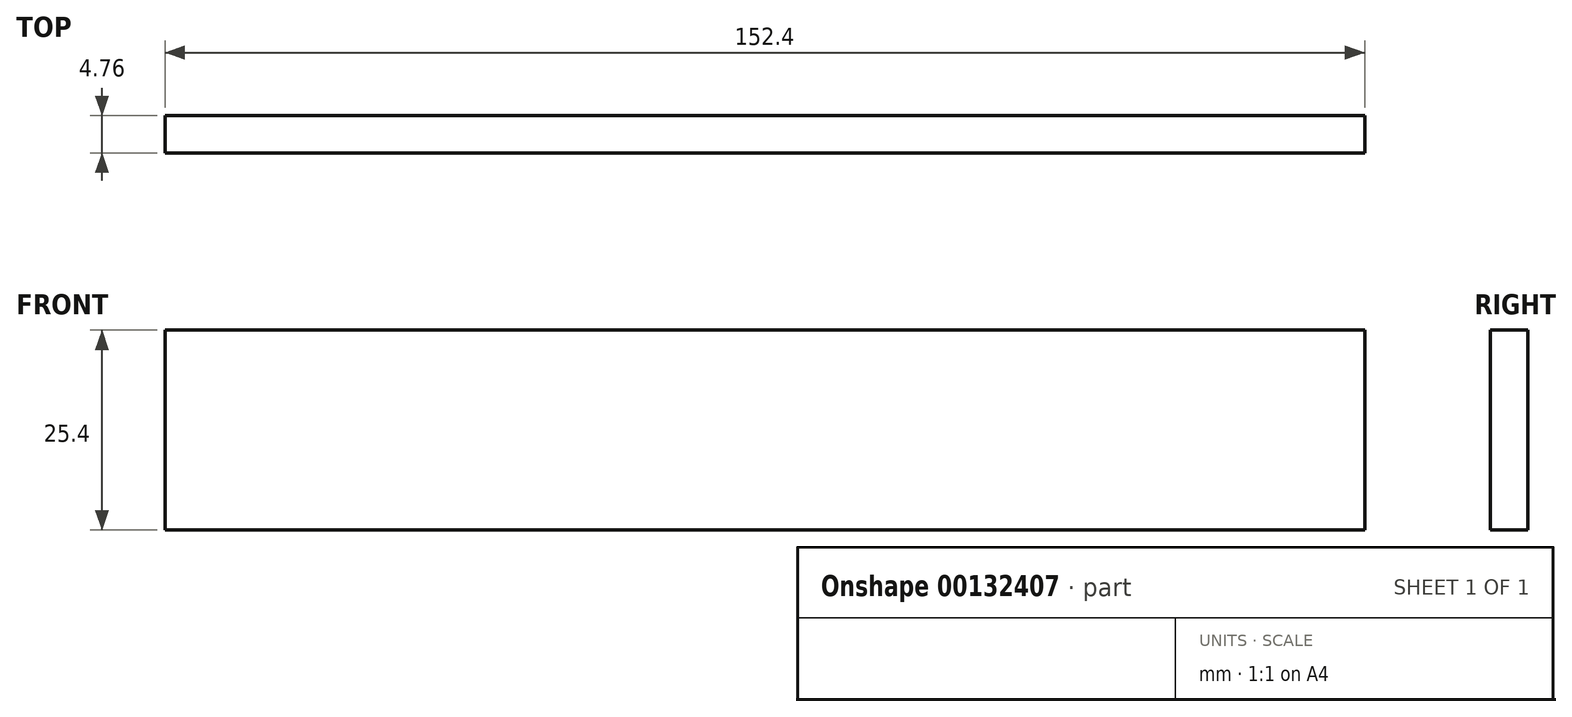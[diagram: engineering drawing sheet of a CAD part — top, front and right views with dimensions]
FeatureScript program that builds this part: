
annotation { "Feature Type Name" : "Feature", "Feature Type Description" : "" }
export const myFeature = defineFeature(function(context is Context, id is Id, definition is map)
    precondition{}
    {
        {
            var Q0;
            Q0=qCreatedBy(makeId("Top.planeOp"),FACE);
            var sketch = newSketch(context, id + "F0", { "sketchPlane" : qUnion([Q0])});
            skLineSegment(sketch, "E0.bottom", {"start": v(-64.4, 36.93) * mm, "end": v(88, 36.93) * mm});
            skLineSegment(sketch, "E0.top", {"start": v(-64.4, 32.17) * mm, "end": v(88, 32.17) * mm});
            skLineSegment(sketch, "E0.left", {"start": v(-64.4, 36.93) * mm, "end": v(-64.4, 32.17) * mm});
            skLineSegment(sketch, "E0.right", {"start": v(88, 36.93) * mm, "end": v(88, 32.17) * mm});
            skSolve(sketch);
        }
        {
            var Q0;
            Q0=makeQuery(id+"F0.imprint","IMPRINT",FACE,{"disambiguationData":[TD([[makeQuery(id+"F0.imprint","IMPRINT",EDGE,{"derivedFrom":sQuery(id+"F0.wireOp",EDGE,"E0.bottom")}),-1.0]])]});
            extrude(context, id + "F1", {"entities" : qUnion([Q0]), "depth" : 25.4 * mm});
        }
    });
